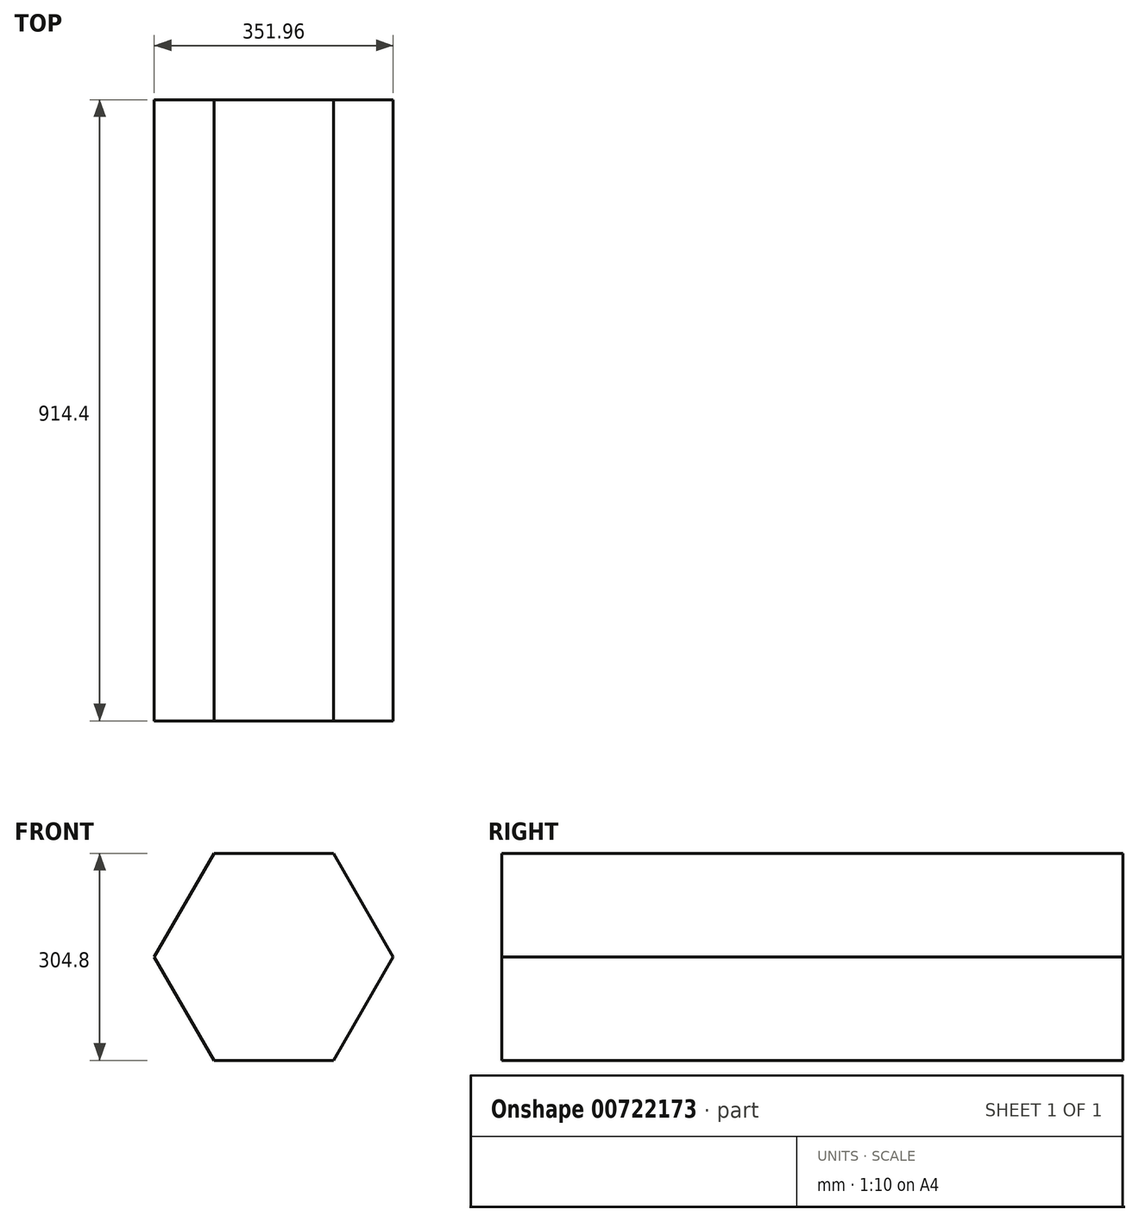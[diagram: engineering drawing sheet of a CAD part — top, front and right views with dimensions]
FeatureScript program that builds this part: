
annotation { "Feature Type Name" : "Feature", "Feature Type Description" : "" }
export const myFeature = defineFeature(function(context is Context, id is Id, definition is map)
    precondition{}
    {
        {
            var Q0;
            Q0=qCreatedBy(makeId("Front.planeOp"),FACE);
            var sketch = newSketch(context, id + "F0", { "sketchPlane" : qUnion([Q0])});
            skCircle(sketch, "E0.cCircle", {"center": v(0, 0) * mm, "radius": 152.4 * mm, "construction": true});
            skLineSegment(sketch, "E0.0", {"start": v(175.98, 0) * mm, "end": v(87.99, -152.4) * mm});
            skLineSegment(sketch, "E0.1", {"start": v(87.99, -152.4) * mm, "end": v(-87.99, -152.4) * mm});
            skLineSegment(sketch, "E0.2", {"start": v(-87.99, -152.4) * mm, "end": v(-175.98, 0) * mm});
            skLineSegment(sketch, "E0.3", {"start": v(-175.98, 0) * mm, "end": v(-87.99, 152.4) * mm});
            skLineSegment(sketch, "E0.4", {"start": v(-87.99, 152.4) * mm, "end": v(87.99, 152.4) * mm});
            skLineSegment(sketch, "E0.5", {"start": v(87.99, 152.4) * mm, "end": v(175.98, 0) * mm});
            skPoint(sketch, "E0.0.midPoint", {"position": v(131.98, -76.2) * mm});
            skSolve(sketch);
        }
        {
            var Q0;
            Q0=qSketchRegion(id+"F0",true);
            extrude(context, id + "F1", {"entities" : qUnion([Q0]), "depth" : 914.4 * mm, "offsetDistance" : 25.4 * mm});
        }
    });
